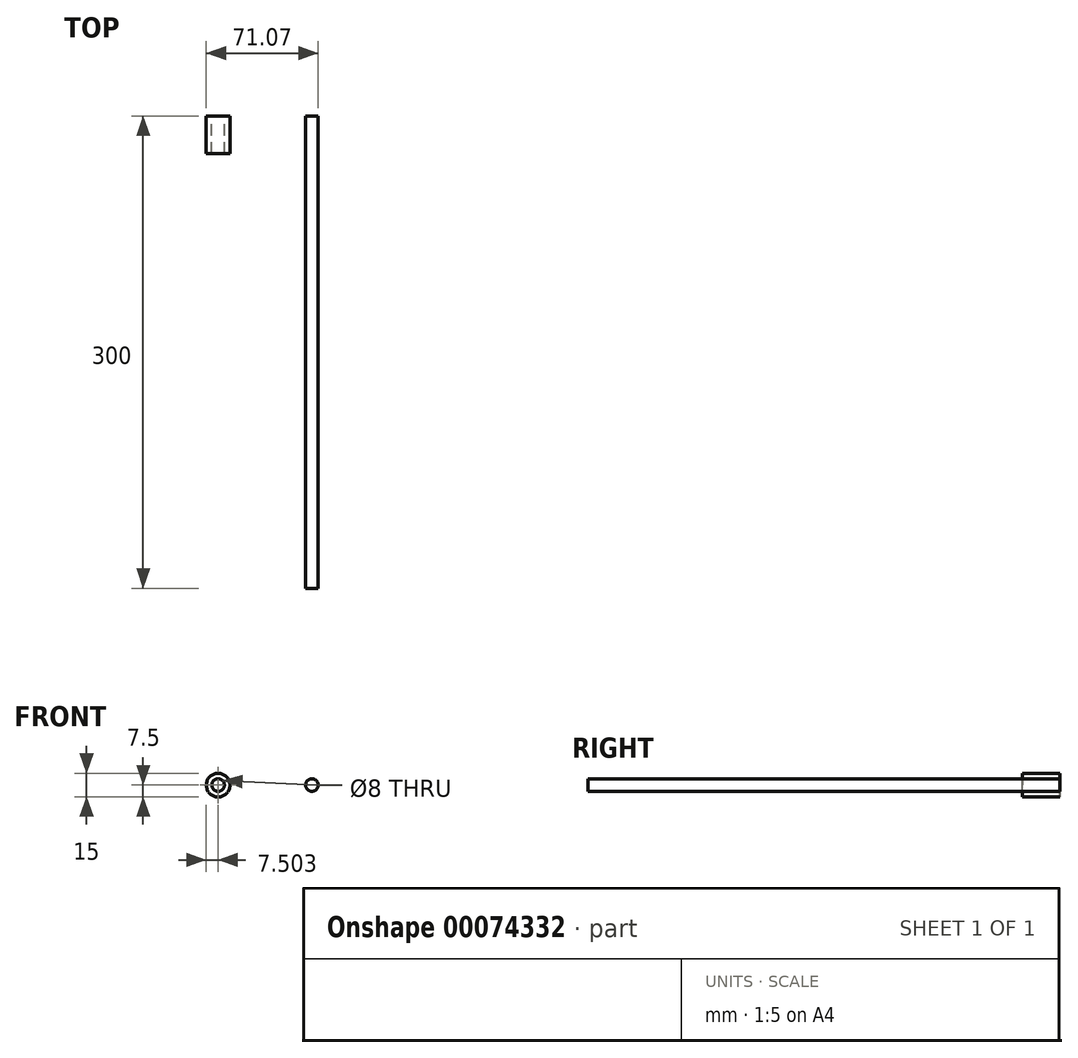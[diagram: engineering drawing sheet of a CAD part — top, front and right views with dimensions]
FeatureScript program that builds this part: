
annotation { "Feature Type Name" : "Feature", "Feature Type Description" : "" }
export const myFeature = defineFeature(function(context is Context, id is Id, definition is map)
    precondition{}
    {
        {
            var Q0;
            Q0=qCreatedBy(makeId("Front.planeOp"),FACE);
            var sketch = newSketch(context, id + "F0", { "sketchPlane" : qUnion([Q0])});
            skCircle(sketch, "E0", {"center": v(28.13, 0) * mm, "radius": 4 * mm});
            skCircle(sketch, "E1", {"center": v(-31.44, 0) * mm, "radius": 4 * mm});
            skCircle(sketch, "E2", {"center": v(-31.44, 0) * mm, "radius": 7.5 * mm});
            skSolve(sketch);
        }
        {
            var Q0;
            Q0=makeQuery(id+"F0.imprint","IMPRINT",FACE,{"disambiguationData":[TD([[makeQuery(id+"F0.imprint","IMPRINT",EDGE,{"derivedFrom":sQuery(id+"F0.wireOp",EDGE,"E1")}),-1.0]])]});
            extrude(context, id + "F1", {"entities" : qUnion([Q0]), "depth" : 24 * mm});
        }
        {
            var Q0;
            Q0=makeQuery(id+"F0.imprint","IMPRINT",FACE,{"disambiguationData":[TD([[makeQuery(id+"F0.imprint","IMPRINT",EDGE,{"derivedFrom":sQuery(id+"F0.wireOp",EDGE,"E0")}),1.0]])]});
            extrude(context, id + "F2", {"entities" : qUnion([Q0]), "depth" : 300 * mm});
        }
    });
